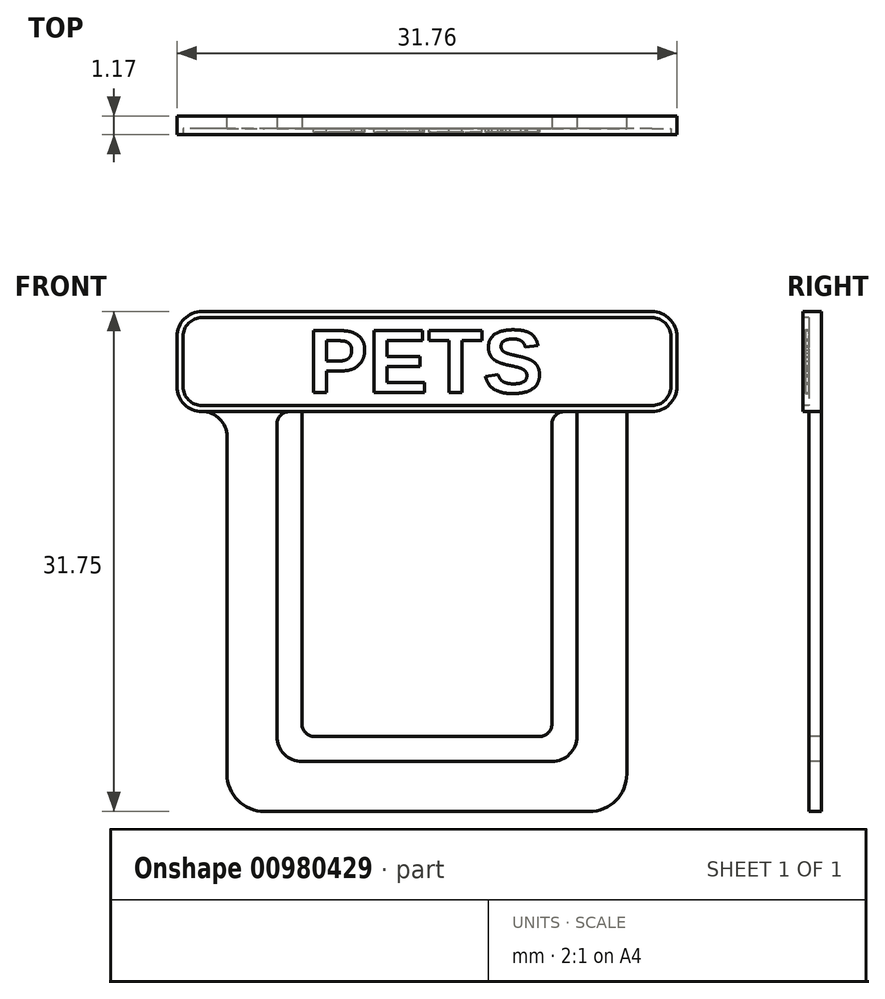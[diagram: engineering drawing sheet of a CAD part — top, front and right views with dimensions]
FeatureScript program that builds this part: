
annotation { "Feature Type Name" : "Feature", "Feature Type Description" : "" }
export const myFeature = defineFeature(function(context is Context, id is Id, definition is map)
    precondition{}
    {
        {
            var Q0;
            Q0=qCreatedBy(makeId("Front.planeOp"),FACE);
            var sketch = newSketch(context, id + "F0", { "sketchPlane" : qUnion([Q0])});
            skLineSegment(sketch, "E0.bottom", {"start": v(12.7, 12.7) * mm, "end": v(-12.7, 12.7) * mm});
            skLineSegment(sketch, "E0.top", {"start": v(12.7, -12.7) * mm, "end": v(-12.7, -12.7) * mm});
            skLineSegment(sketch, "E0.left", {"start": v(12.7, 12.7) * mm, "end": v(12.7, -12.7) * mm});
            skLineSegment(sketch, "E0.right", {"start": v(-12.7, 12.7) * mm, "end": v(-12.7, -12.7) * mm});
            skPoint(sketch, "E0.middle", {"position": v(0, 0) * mm});
            skSolve(sketch);
        }
        {
            var Q0;
            Q0=makeQuery(id+"F0.imprint","IMPRINT",FACE,{"disambiguationData":[TD([[makeQuery(id+"F0.imprint","IMPRINT",EDGE,{"derivedFrom":sQuery(id+"F0.wireOp",EDGE,"E0.bottom")}),1.0]])]});
            extrude(context, id + "F1", {"entities" : qUnion([Q0]), "depth" : 0.8 * mm, "offsetDistance" : 25.4 * mm});
        }
        {
            var Q0;
            Q0=makeQuery(id+"F1.opExtrude","SWEPT_EDGE",EDGE,{"disambiguationData":[OSD([sQuery(id+"F0.wireOp",EDGE,"E0.top"),sQuery(id+"F0.wireOp",EDGE,"E0.left")])]});
            var Q1;
            Q1=makeQuery(id+"F1.opExtrude","SWEPT_EDGE",EDGE,{"disambiguationData":[OSD([sQuery(id+"F0.wireOp",EDGE,"E0.top"),sQuery(id+"F0.wireOp",EDGE,"E0.right")])]});
            fillet(context, id + "F2", {"entities" : qUnion([Q0, Q1]), "radius" : 2.38 * mm, "tangentPropagation" : true, "allowEdgeOverflow" : false});
        }
        {
            var Q0;
            Q0=makeQuery(id+"F1.opExtrude","CAP_FACE",FACE,{"disambiguationData":[OSD([sQuery(id+"F0.wireOp",EDGE,"E0.bottom"),sQuery(id+"F0.wireOp",EDGE,"E0.top"),sQuery(id+"F0.wireOp",EDGE,"E0.left"),sQuery(id+"F0.wireOp",EDGE,"E0.right")])],"isStart":false});
            var sketch = newSketch(context, id + "F3", { "sketchPlane" : qUnion([Q0])});
            skLineSegment(sketch, "E1.bottom", {"start": v(9.52, 12.7) * mm, "end": v(-9.53, 12.7) * mm});
            skLineSegment(sketch, "E1.top", {"start": v(9.53, -9.53) * mm, "end": v(-9.52, -9.53) * mm});
            skLineSegment(sketch, "E1.left", {"start": v(9.52, 12.7) * mm, "end": v(9.53, -9.53) * mm});
            skLineSegment(sketch, "E1.right", {"start": v(-9.53, 12.7) * mm, "end": v(-9.52, -9.53) * mm});
            skPoint(sketch, "E1.middle", {"position": v(0, 0) * mm});
            skSolve(sketch);
        }
        {
            var Q0;
            Q0=makeQuery(id+"F3.imprint","IMPRINT",FACE,{"disambiguationData":[TD([[makeQuery(id+"F3.imprint","IMPRINT",EDGE,{"derivedFrom":sQuery(id+"F3.wireOp",EDGE,"E1.bottom")}),1.0]])]});
            extrude(context, id + "F4", {"entities" : qUnion([Q0]), "operationType" : NewBodyOperationType.REMOVE, "oppositeDirection" : true, "depth" : 4.93 * mm, "offsetDistance" : 25.4 * mm});
        }
        {
            var Q0;
            Q0=makeQuery(id+"F1.opExtrude","CAP_FACE",FACE,{"disambiguationData":[OSD([sQuery(id+"F0.wireOp",EDGE,"E0.bottom"),sQuery(id+"F0.wireOp",EDGE,"E0.top"),sQuery(id+"F0.wireOp",EDGE,"E0.left"),sQuery(id+"F0.wireOp",EDGE,"E0.right")])],"isStart":false});
            var sketch = newSketch(context, id + "F5", { "sketchPlane" : qUnion([Q0])});
            skLineSegment(sketch, "E2.bottom", {"start": v(-15.88, 12.7) * mm, "end": v(15.88, 12.7) * mm});
            skLineSegment(sketch, "E2.top", {"start": v(-15.88, 19.05) * mm, "end": v(15.88, 19.05) * mm});
            skLineSegment(sketch, "E2.left", {"start": v(-15.88, 12.7) * mm, "end": v(-15.88, 19.05) * mm});
            skLineSegment(sketch, "E2.right", {"start": v(15.87, 12.7) * mm, "end": v(15.87, 19.05) * mm});
            skSolve(sketch);
        }
        {
            var Q0;
            Q0=makeQuery(id+"F5.imprint","IMPRINT",FACE,{"disambiguationData":[TD([[makeQuery(id+"F5.imprint","IMPRINT",EDGE,{"derivedFrom":sQuery(id+"F5.wireOp",EDGE,"E2.top")}),-1.0]])]});
            extrude(context, id + "F6", {"entities" : qUnion([Q0]), "operationType" : NewBodyOperationType.ADD, "oppositeDirection" : true, "depth" : 0.8 * mm, "offsetDistance" : 25.4 * mm});
        }
        {
            var Q0;
            Q0=makeQuery(id+"F6.opExtrude","SWEPT_EDGE",EDGE,{"disambiguationData":[OSD([sQuery(id+"F5.wireOp",EDGE,"E2.top"),sQuery(id+"F5.wireOp",EDGE,"E2.left")])]});
            var Q1;
            Q1=makeQuery(id+"F6.opExtrude","SWEPT_EDGE",EDGE,{"disambiguationData":[OSD([sQuery(id+"F5.wireOp",EDGE,"E2.top"),sQuery(id+"F5.wireOp",EDGE,"E2.right")])]});
            var Q2;
            Q2=makeQuery(id+"F6.opExtrude","SWEPT_EDGE",EDGE,{"disambiguationData":[OSD([sQuery(id+"F5.wireOp",EDGE,"E2.bottom"),sQuery(id+"F5.wireOp",EDGE,"E2.right")])]});
            var Q3;
            Q3=makeQuery(id+"F1.opExtrude","SWEPT_EDGE",EDGE,{"disambiguationData":[OSD([sQuery(id+"F0.wireOp",EDGE,"E0.bottom"),sQuery(id+"F0.wireOp",EDGE,"E0.left")])]});
            var Q4;
            Q4=makeQuery(id+"F6.opExtrude","SWEPT_EDGE",EDGE,{"disambiguationData":[OSD([sQuery(id+"F5.wireOp",EDGE,"E2.bottom"),sQuery(id+"F5.wireOp",EDGE,"E2.left")])]});
            var Q5;
            Q5=makeQuery(id+"F1.opExtrude","SWEPT_EDGE",EDGE,{"disambiguationData":[OSD([sQuery(id+"F0.wireOp",EDGE,"E0.bottom"),sQuery(id+"F0.wireOp",EDGE,"E0.right")])]});
            fillet(context, id + "F7", {"entities" : qUnion([Q0, Q1, Q2, Q3, Q4, Q5]), "radius" : 1.59 * mm, "tangentPropagation" : true, "allowEdgeOverflow" : false});
        }
        {
            var Q0;
            Q0=makeQuery(id+"F4.boolean.opBoolean","COPY",EDGE,{"derivedFrom":makeQuery(id+"F4.opExtrude","SWEPT_EDGE",EDGE,{"disambiguationData":[OSD([sQuery(id+"F3.wireOp",EDGE,"E1.top"),sQuery(id+"F3.wireOp",EDGE,"E1.right")])]})});
            var Q1;
            Q1=makeQuery(id+"F4.boolean.opBoolean","COPY",EDGE,{"derivedFrom":makeQuery(id+"F4.opExtrude","SWEPT_EDGE",EDGE,{"disambiguationData":[OSD([sQuery(id+"F3.wireOp",EDGE,"E1.top"),sQuery(id+"F3.wireOp",EDGE,"E1.left")])]})});
            fillet(context, id + "F8", {"entities" : qUnion([Q0, Q1]), "radius" : 1.59 * mm, "tangentPropagation" : true, "allowEdgeOverflow" : false});
        }
        {
            var Q0;
            Q0=makeQuery(id+"F6.boolean.opBoolean","MERGE",FACE,{"derivedFrom":[makeQuery(id+"F1.opExtrude","CAP_FACE",FACE,{"disambiguationData":[OSD([sQuery(id+"F0.wireOp",EDGE,"E0.bottom"),sQuery(id+"F0.wireOp",EDGE,"E0.top"),sQuery(id+"F0.wireOp",EDGE,"E0.left"),sQuery(id+"F0.wireOp",EDGE,"E0.right")])],"isStart":false}),makeQuery(id+"F6.opExtrude","CAP_FACE",FACE,{"disambiguationData":[OSD([sQuery(id+"F5.wireOp",EDGE,"E2.bottom"),sQuery(id+"F5.wireOp",EDGE,"E2.top"),sQuery(id+"F5.wireOp",EDGE,"E2.left"),sQuery(id+"F5.wireOp",EDGE,"E2.right")])],"isStart":true})]});
            var sketch = newSketch(context, id + "F9", { "sketchPlane" : qUnion([Q0])});
            skLineSegment(sketch, "E3.bottom", {"start": v(-7.94, 12.7) * mm, "end": v(7.94, 12.7) * mm});
            skLineSegment(sketch, "E3.top", {"start": v(-7.94, -7.94) * mm, "end": v(7.94, -7.94) * mm});
            skLineSegment(sketch, "E3.left", {"start": v(-7.94, 12.7) * mm, "end": v(-7.94, -7.94) * mm});
            skLineSegment(sketch, "E3.right", {"start": v(7.94, 12.7) * mm, "end": v(7.94, -7.94) * mm});
            skSolve(sketch);
        }
        {
            var Q0;
            Q0=makeQuery(id+"F9.imprint","IMPRINT",FACE,{"disambiguationData":[TD([[makeQuery(id+"F9.imprint","IMPRINT",EDGE,{"derivedFrom":sQuery(id+"F9.wireOp",EDGE,"E3.bottom")}),1.0]])]});
            extrude(context, id + "F10", {"entities" : qUnion([Q0]), "operationType" : NewBodyOperationType.ADD, "oppositeDirection" : true, "depth" : 0.8 * mm, "offsetDistance" : 25.4 * mm});
        }
        {
            var Q0;
            Q0=makeQuery(id+"F10.opExtrude","SWEPT_EDGE",EDGE,{"disambiguationData":[OSD([sQuery(id+"F5.wireOp",EDGE,"E2.bottom"),sQuery(id+"F9.wireOp",EDGE,"E3.bottom"),sQuery(id+"F9.wireOp",EDGE,"E3.left")])]});
            var Q1;
            Q1=makeQuery(id+"F4.boolean.opBoolean","COPY",EDGE,{"derivedFrom":makeQuery(id+"F4.opExtrude","SWEPT_EDGE",EDGE,{"disambiguationData":[OSD([sQuery(id+"F0.wireOp",EDGE,"E0.bottom"),sQuery(id+"F3.wireOp",EDGE,"E1.bottom"),sQuery(id+"F3.wireOp",EDGE,"E1.right")])]})});
            var Q2;
            Q2=makeQuery(id+"F10.opExtrude","SWEPT_EDGE",EDGE,{"disambiguationData":[OSD([sQuery(id+"F5.wireOp",EDGE,"E2.bottom"),sQuery(id+"F9.wireOp",EDGE,"E3.bottom"),sQuery(id+"F9.wireOp",EDGE,"E3.right")])]});
            var Q3;
            Q3=makeQuery(id+"F4.boolean.opBoolean","COPY",EDGE,{"derivedFrom":makeQuery(id+"F4.opExtrude","SWEPT_EDGE",EDGE,{"disambiguationData":[OSD([sQuery(id+"F0.wireOp",EDGE,"E0.bottom"),sQuery(id+"F3.wireOp",EDGE,"E1.bottom"),sQuery(id+"F3.wireOp",EDGE,"E1.left")])]})});
            fillet(context, id + "F11", {"entities" : qUnion([Q0, Q1, Q2, Q3]), "radius" : 0.8 * mm, "tangentPropagation" : true, "allowEdgeOverflow" : false});
        }
        {
            var Q0;
            Q0=makeQuery(id+"F10.opExtrude","SWEPT_EDGE",EDGE,{"disambiguationData":[OSD([sQuery(id+"F9.wireOp",EDGE,"E3.top"),sQuery(id+"F9.wireOp",EDGE,"E3.left")])]});
            var Q1;
            Q1=makeQuery(id+"F10.opExtrude","SWEPT_EDGE",EDGE,{"disambiguationData":[OSD([sQuery(id+"F9.wireOp",EDGE,"E3.top"),sQuery(id+"F9.wireOp",EDGE,"E3.right")])]});
            fillet(context, id + "F12", {"entities" : qUnion([Q0, Q1]), "radius" : 0.8 * mm, "tangentPropagation" : true, "allowEdgeOverflow" : false});
        }
        {
            var Q0;
            Q0=makeQuery(id+"F10.boolean.opBoolean","MERGE",FACE,{"derivedFrom":[makeQuery(id+"F6.boolean.opBoolean","MERGE",FACE,{"derivedFrom":[makeQuery(id+"F1.opExtrude","CAP_FACE",FACE,{"disambiguationData":[OSD([sQuery(id+"F0.wireOp",EDGE,"E0.bottom"),sQuery(id+"F0.wireOp",EDGE,"E0.top"),sQuery(id+"F0.wireOp",EDGE,"E0.left"),sQuery(id+"F0.wireOp",EDGE,"E0.right")])],"isStart":false}),makeQuery(id+"F6.opExtrude","CAP_FACE",FACE,{"disambiguationData":[OSD([sQuery(id+"F5.wireOp",EDGE,"E2.bottom"),sQuery(id+"F5.wireOp",EDGE,"E2.top"),sQuery(id+"F5.wireOp",EDGE,"E2.left"),sQuery(id+"F5.wireOp",EDGE,"E2.right")])],"isStart":true})]}),makeQuery(id+"F10.opExtrude","CAP_FACE",FACE,{"disambiguationData":[OSD([sQuery(id+"F9.wireOp",EDGE,"E3.bottom"),sQuery(id+"F9.wireOp",EDGE,"E3.top"),sQuery(id+"F9.wireOp",EDGE,"E3.left"),sQuery(id+"F9.wireOp",EDGE,"E3.right")])],"isStart":true})]});
            var sketch = newSketch(context, id + "F13", { "sketchPlane" : qUnion([Q0])});
            skArc(sketch, "E4.0", {"start": v(-14.29, 19.05) * mm, "mid": v(-15.41, 18.59) * mm, "end": v(-15.88, 17.46) * mm});
            skLineSegment(sketch, "E5.0", {"start": v(-15.88, 14.29) * mm, "end": v(-15.88, 17.46) * mm});
            skArc(sketch, "E6.0", {"start": v(-15.88, 14.29) * mm, "mid": v(-15.41, 13.16) * mm, "end": v(-14.29, 12.7) * mm});
            skLineSegment(sketch, "E7.0", {"start": v(-14.29, 19.05) * mm, "end": v(14.29, 19.05) * mm});
            skArc(sketch, "E8.0", {"start": v(15.87, 17.46) * mm, "mid": v(15.41, 18.59) * mm, "end": v(14.29, 19.05) * mm});
            skLineSegment(sketch, "E9.0", {"start": v(15.87, 14.29) * mm, "end": v(15.87, 17.46) * mm});
            skArc(sketch, "E10.0", {"start": v(14.29, 12.7) * mm, "mid": v(15.41, 13.16) * mm, "end": v(15.87, 14.29) * mm});
            skLineSegment(sketch, "E11", {"start": v(-14.29, 12.7) * mm, "end": v(14.29, 12.7) * mm});
            skSolve(sketch);
        }
        {
            var Q0;
            Q0=makeQuery(id+"F13.imprint","IMPRINT",FACE,{"disambiguationData":[TD([[makeQuery(id+"F13.imprint","IMPRINT",EDGE,{"derivedFrom":sQuery(id+"F13.wireOp",EDGE,"E4.0")}),1.0]])]});
            extrude(context, id + "F14", {"entities" : qUnion([Q0]), "operationType" : NewBodyOperationType.ADD, "depth" : 0.38 * mm, "offsetDistance" : 25.4 * mm});
        }
        {
            var Q0;
            Q0=makeQuery(id+"F14.opExtrude","CAP_FACE",FACE,{"disambiguationData":[OSD([sQuery(id+"F13.wireOp",EDGE,"E4.0"),sQuery(id+"F13.wireOp",EDGE,"E5.0"),sQuery(id+"F13.wireOp",EDGE,"E6.0"),sQuery(id+"F13.wireOp",EDGE,"E7.0"),sQuery(id+"F13.wireOp",EDGE,"E8.0"),sQuery(id+"F13.wireOp",EDGE,"E9.0"),sQuery(id+"F13.wireOp",EDGE,"E10.0"),sQuery(id+"F13.wireOp",EDGE,"E11")])],"isStart":false});
            var sketch = newSketch(context, id + "F15", { "sketchPlane" : qUnion([Q0])});
            skArc(sketch, "E12.0", {"start": v(-14.29, 19.05) * mm, "mid": v(-15.41, 18.59) * mm, "end": v(-15.88, 17.46) * mm});
            skLineSegment(sketch, "E13.0", {"start": v(-14.29, 19.05) * mm, "end": v(14.29, 19.05) * mm});
            skLineSegment(sketch, "E14.0", {"start": v(-15.88, 14.29) * mm, "end": v(-15.88, 17.46) * mm});
            skArc(sketch, "E15.0", {"start": v(-15.88, 14.29) * mm, "mid": v(-15.41, 13.16) * mm, "end": v(-14.29, 12.7) * mm});
            skLineSegment(sketch, "E16.0", {"start": v(-14.29, 12.7) * mm, "end": v(14.29, 12.7) * mm});
            skArc(sketch, "E17.0", {"start": v(14.29, 12.7) * mm, "mid": v(15.41, 13.16) * mm, "end": v(15.87, 14.29) * mm});
            skArc(sketch, "E18.0", {"start": v(15.87, 17.46) * mm, "mid": v(15.41, 18.59) * mm, "end": v(14.29, 19.05) * mm});
            skArc(sketch, "E19", {"start": v(-14.29, 18.67) * mm, "mid": v(-15.14, 18.32) * mm, "end": v(-15.5, 17.46) * mm});
            skArc(sketch, "E20", {"start": v(-15.5, 14.29) * mm, "mid": v(-15.14, 13.43) * mm, "end": v(-14.29, 13.08) * mm});
            skArc(sketch, "E21", {"start": v(15.5, 17.46) * mm, "mid": v(15.14, 18.32) * mm, "end": v(14.29, 18.67) * mm});
            skArc(sketch, "E22", {"start": v(14.29, 13.08) * mm, "mid": v(15.14, 13.43) * mm, "end": v(15.5, 14.29) * mm});
            skLineSegment(sketch, "E23", {"start": v(-14.29, 19.05) * mm, "end": v(-14.29, 12.7) * mm, "construction": true});
            skLineSegment(sketch, "E24", {"start": v(-15.88, 17.46) * mm, "end": v(15.87, 17.46) * mm, "construction": true});
            skLineSegment(sketch, "E25", {"start": v(14.29, 19.05) * mm, "end": v(14.29, 12.7) * mm, "construction": true});
            skLineSegment(sketch, "E26", {"start": v(15.87, 14.29) * mm, "end": v(-15.88, 14.29) * mm, "construction": true});
            skLineSegment(sketch, "E27", {"start": v(14.29, 18.67) * mm, "end": v(-14.29, 18.67) * mm});
            skLineSegment(sketch, "E28", {"start": v(-15.5, 17.46) * mm, "end": v(-15.5, 14.29) * mm});
            skLineSegment(sketch, "E29", {"start": v(-14.29, 13.08) * mm, "end": v(14.29, 13.08) * mm});
            skLineSegment(sketch, "E30", {"start": v(15.5, 17.46) * mm, "end": v(15.5, 14.29) * mm});
            skSolve(sketch);
        }
        {
            var Q0;
            Q0=makeQuery(id+"F15.imprint","IMPRINT",FACE,{"disambiguationData":[TD([[makeQuery(id+"F15.imprint","IMPRINT",EDGE,{"derivedFrom":sQuery(id+"F15.wireOp",EDGE,"E19")}),1.0]])]});
            var Q1;
            {var subQ0=sQuery(id+"F9.wireOp",EDGE,"E3.right");var subQ1=sQuery(id+"F9.wireOp",EDGE,"E3.top");var subQ3=sQuery(id+"F0.wireOp",EDGE,"E0.bottom");var subQ4=sQuery(id+"F9.wireOp",EDGE,"E3.left");var subQ5=makeQuery(id+"F6.opExtrude","CAP_FACE",FACE,{"disambiguationData":[OSD([sQuery(id+"F5.wireOp",EDGE,"E2.bottom"),sQuery(id+"F5.wireOp",EDGE,"E2.top"),sQuery(id+"F5.wireOp",EDGE,"E2.left"),sQuery(id+"F5.wireOp",EDGE,"E2.right")])],"isStart":true});var subQ6=makeQuery(id+"F1.opExtrude","CAP_FACE",FACE,{"disambiguationData":[OSD([subQ3,sQuery(id+"F0.wireOp",EDGE,"E0.top"),sQuery(id+"F0.wireOp",EDGE,"E0.left"),sQuery(id+"F0.wireOp",EDGE,"E0.right")])],"isStart":false});var subQ7=makeQuery(id+"F10.opExtrude","CAP_FACE",FACE,{"disambiguationData":[OSD([sQuery(id+"F9.wireOp",EDGE,"E3.bottom"),subQ1,subQ4,subQ0])],"isStart":true});Q1=makeQuery(id+"F14.boolean.opBoolean","SPLIT",FACE,{"disambiguationData":[TD([makeQuery(id+"F10.opExtrude","SWEPT_FACE",FACE,{"disambiguationData":[OSD([subQ1])]})])],"derivedFrom":makeQuery(id+"F10.boolean.opBoolean","MERGE",FACE,{"derivedFrom":[makeQuery(id+"F6.boolean.opBoolean","MERGE",FACE,{"derivedFrom":[subQ6,subQ5]}),subQ7]})});}
            extrude(context, id + "F16", {"entities" : qUnion([Q0]), "operationType" : NewBodyOperationType.REMOVE, "endBound" : BoundingType.UP_TO_SURFACE, "oppositeDirection" : true, "depth" : 25.4 * mm, "endBoundEntityFace" : qUnion([Q1]), "offsetDistance" : 25.4 * mm});
        }
        {
            var Q0;
            Q0=qCreatedBy(makeId("Front.planeOp"),FACE);
            var sketch = newSketch(context, id + "F17", { "sketchPlane" : qUnion([Q0])});
            skText(sketch, "E31", { "text": "PETS", "fontName": "Arimo-Bold.ttf"});
            const initialGuessF17  = {"E31": [-0.00757, 0.0139, 1, 0, 0.00412]};
            skSetInitialGuess(sketch, initialGuessF17);
            skSolve(sketch);
        }
        {
            var Q0;
            Q0=qSketchRegion(id+"F17",true);
            extrude(context, id + "F18", {"entities" : qUnion([Q0]), "operationType" : NewBodyOperationType.ADD, "depth" : 1.02 * mm, "offsetDistance" : 25.4 * mm});
        }
    });
